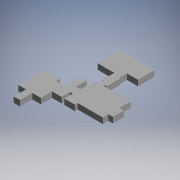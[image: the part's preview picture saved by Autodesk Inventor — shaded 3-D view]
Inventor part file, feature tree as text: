
AUTODESK INVENTOR PART (.ipt)
format: ipt  version: 2019.4 (Build 234330000, 330)  size: 141,312 bytes
history: native  units: mm (DEFAULTED — no unit token found)
features: extrude x1, sketch x1
ambient origin geometry x8: Origin, YZ Plane, XZ Plane, XY Plane, X Axis, Y Axis, Z Axis, Center Point
bodies: Solid1 (feature_tree)
feature tree (2):
  extrude  "Extrusion1"  Depth=800.0mm
  sketch  "Sketch1"  dims[d0=2000.0mm d1=800.0mm d2=1000.0mm d3=6400.0mm d4=1000.0mm d5=1400.0mm d6=2000.0mm d7=700.0mm d8=800.0mm d9=500.0mm d10=1500.0mm d11=1700.0mm d12=2000.0mm d13=1550.0mm d14=1100.0mm d15=800.0mm d16=1900.0mm d17=1200.0mm d18=2800.0mm d19=1450.0mm d20=700.0mm d21=2800.0mm d22=2200.0mm d23=850.0mm d24=200.0mm d25=2100.0mm d26=3000.0mm d27=4000.0mm d28=200.0mm d29=400.0mm d30=2450.0mm d31=200.0mm d32=1350.0mm d33=2000.0mm d34=1000.0mm d35=0.0mm]
